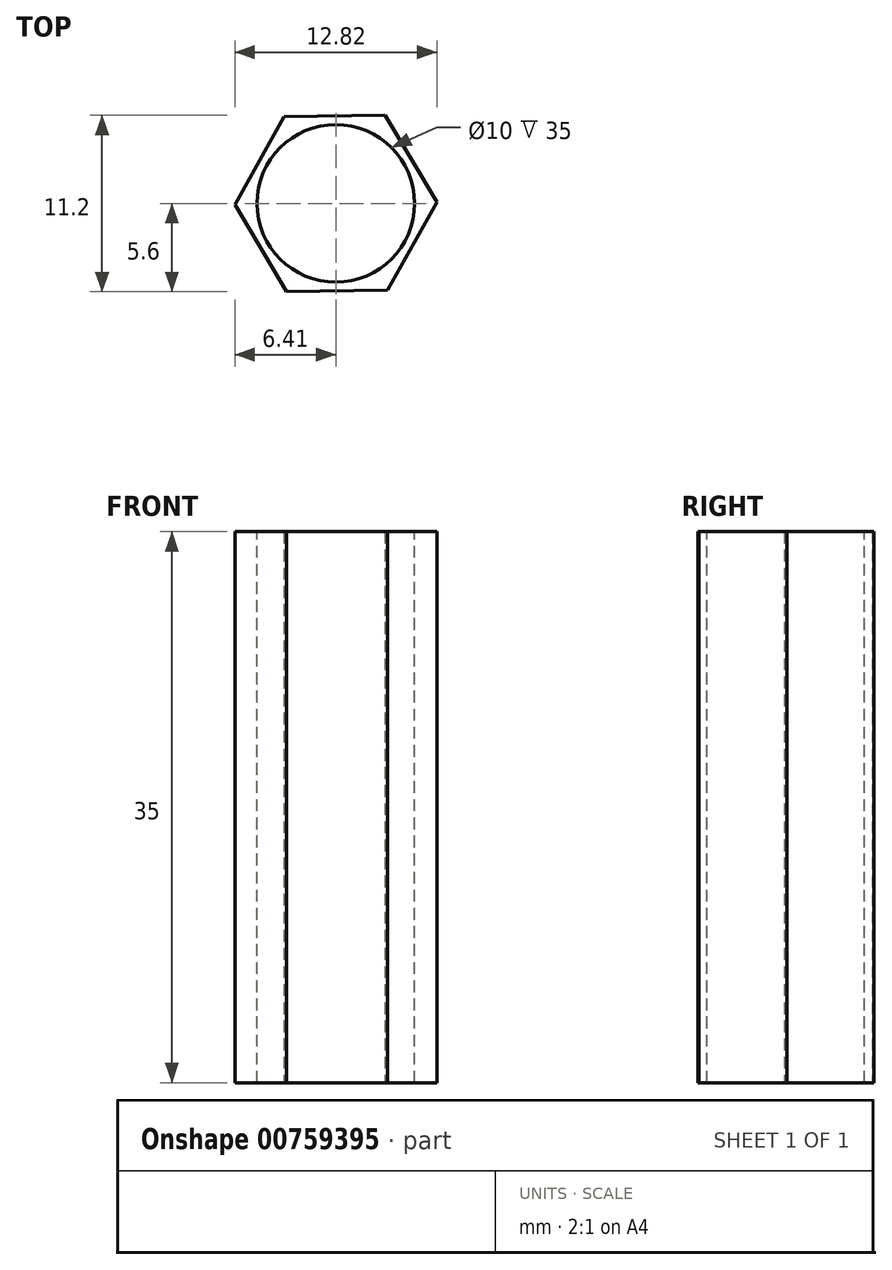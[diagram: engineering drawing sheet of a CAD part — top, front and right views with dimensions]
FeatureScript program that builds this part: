
annotation { "Feature Type Name" : "Feature", "Feature Type Description" : "" }
export const myFeature = defineFeature(function(context is Context, id is Id, definition is map)
    precondition{}
    {
        {
            var Q0;
            Q0=qCreatedBy(makeId("Top.planeOp"),FACE);
            var sketch = newSketch(context, id + "F0", { "sketchPlane" : qUnion([Q0])});
            skCircle(sketch, "E0.cCircle", {"center": v(0, 0) * mm, "radius": 5.55 * mm, "construction": true});
            skLineSegment(sketch, "E0.0", {"start": v(-6.41, -0.08) * mm, "end": v(-3.28, 5.51) * mm});
            skLineSegment(sketch, "E0.1", {"start": v(-3.28, 5.51) * mm, "end": v(3.14, 5.6) * mm});
            skLineSegment(sketch, "E0.2", {"start": v(3.14, 5.6) * mm, "end": v(6.41, 0.08) * mm});
            skLineSegment(sketch, "E0.3", {"start": v(6.41, 0.08) * mm, "end": v(3.28, -5.51) * mm});
            skLineSegment(sketch, "E0.4", {"start": v(3.28, -5.51) * mm, "end": v(-3.14, -5.6) * mm});
            skLineSegment(sketch, "E0.5", {"start": v(-3.14, -5.6) * mm, "end": v(-6.41, -0.08) * mm});
            skPoint(sketch, "E0.0.midPoint", {"position": v(-4.85, 2.72) * mm});
            skSolve(sketch);
        }
        {
            var Q0;
            Q0 = qSketchRegion(id + "F0", true);
            extrude(context, id + "F1", {"entities" : qUnion([Q0]), "depth" : 35 * mm, "offsetDistance" : 25 * mm});
        }
        {
            var Q0;
            Q0=makeQuery(id+"F1.opExtrude","CAP_FACE",FACE,{"disambiguationData":[OSD([sQuery(id+"F0.wireOp",EDGE,"E0.0"),sQuery(id+"F0.wireOp",EDGE,"E0.1"),sQuery(id+"F0.wireOp",EDGE,"E0.2"),sQuery(id+"F0.wireOp",EDGE,"E0.3"),sQuery(id+"F0.wireOp",EDGE,"E0.4"),sQuery(id+"F0.wireOp",EDGE,"E0.5")])],"isStart":false});
            var sketch = newSketch(context, id + "F2", { "sketchPlane" : qUnion([Q0])});
            skCircle(sketch, "E1", {"center": v(0, 0) * mm, "radius": 5 * mm});
            skSolve(sketch);
        }
        {
            var Q0;
            Q0 = qSketchRegion(id + "F2", true);
            var Q1;
            Q1=makeQuery(id+"F2.imprint","IMPRINT",FACE,{"disambiguationData":[TD([[makeQuery(id+"F2.imprint","IMPRINT",EDGE,{"derivedFrom":sQuery(id+"F2.wireOp",EDGE,"E1")}),1.0]])]});
            extrude(context, id + "F3", {"entities" : qUnion([Q0, Q1]), "operationType" : NewBodyOperationType.REMOVE, "oppositeDirection" : true, "depth" : 35 * mm, "offsetDistance" : 25 * mm});
        }
    });
